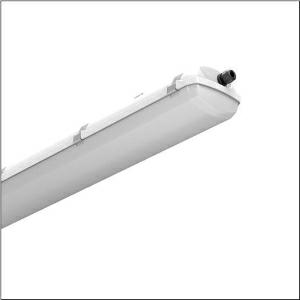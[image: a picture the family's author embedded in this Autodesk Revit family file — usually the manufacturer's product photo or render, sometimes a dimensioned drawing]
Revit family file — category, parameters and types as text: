
# Revit family: monsun_r__ex_51fxb1dp4d0a_11b9
name_source: partatom
category: Lighting Fixtures
units: mm (PartAtom-declared; Revit-internal decimal feet)

## family parameters
Cut with Voids When Loaded = No
Host = Face
Light Source = No
Part Type = Normal
Room Calculation Point = No
Round Connector Dimension = Use Diameter
Shared = No

## types (1)
- Monsun® Ex (1 x LED, 17900 lm, 116.3 W, 4000K)
    Apparent Load = 116 VA
    CIE Flux Codes = 61 86 97 98 100
    Color Rendering = 80
    Color Temperature = 4000K
    Default Elevation = 1800 mm
    Description = Monsun® Ex, damp-proof luminaire, primary optical cover: cover, of PC, UV-stabilised, opal, light emission: direct distribution, primary light characteristic: symmetric, installation type: surface-mounted, LED, rated luminous flux: 17.900lm, luminous efficacy: 154lm/W, light colour: 840, colour temperature: 4000K, control gear: DALI 2, with terminal, 5-pole, max. 2.5mm², through-wiring: 7x 2.5mm², mains connection: 220..240V, AC, 50/60Hz, rated input power: 116W, housing, of PC, light grey (RAL 7035), incl. blind plug, incl. 1x Ex cable gland M20 for cable diameter 7..12mm with sealing, length: 1.580mm, width: 155mm, height: 105mm, clip for enclosure, of stainless steel, protection rating (complete): IP66, insulation class (complete): insulation class I (protective earthing), certification: CE, explosion class: zone2,22 II 3G Ex nR IIC T6 GC, II 3D Ex tc IIIC T80°C Dc, impact resistance: IK10, permissible operating ambient temperature: -20..+40°C, LABS conformity tested according to VDMA 24364:2018-05, contact your sales advisor before using the luminaires in applications with unclear chemical exposure, large temperature fluctuations or condensation-forming humidity, packaging unit: 1 piece
    Height = 105 mm
    Lamp = 1 x LED
    Lamp Light Flux = 17900 lm
    Lamp Power = 116.3 W
    Lamp count = 1
    Length = 1580 mm
    Luminous efficacy = 154 lm/W
    Manufacturer = Siteco
    ModVariant = No
    Model = 51FXB1DP4D0A
    Mounting Place = Ceiling
    Mounting Type = Surface mounted
    Number of Poles = 1
    OnlyDefault = Yes
    Power Factor = 1
    Product Name = Monsun® Ex
    Product group = damp-proof luminaire
    ProductGroupID = 300
    Protection Class = Protection class I
    Protection Degree = IP 66
    RLX_Detail_Level = 1
    RLX_Emergency_Light_Flux = 0 lm
    RLX_Emergency_Type = 0
    RLX_Emergency_Type_DB = No
    RlxData = <blob elided: 41785 chars, md5=c65c3017>
    Socket = socket
    Standby Power = 0 W
    System Light Flux = 17900 lm
    System Power = 116 W
    Type Comments = Product without accessories
    Type Image = l_1258882.jpg
    URL = http://relux.com
    VarID = ---
    Voltage = 0 V
    Weight = 0.00 kg
    Width = 155 mm

## geometry (parser evidence)
native form markers: Blend x4, Sweep x7
no freeform markers — native parametric forms only
